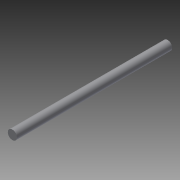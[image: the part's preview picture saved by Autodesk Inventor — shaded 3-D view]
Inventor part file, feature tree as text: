
AUTODESK INVENTOR PART (.ipt)
format: ipt  version: 2014 (Build 180170000, 170)  size: 65,536 bytes
history: native  units: mm
features: extrude x1, sketch x1
ambient origin geometry x8: Origin, YZ Plane, XZ Plane, XY Plane, X Axis, Y Axis, Z Axis, Center Point
bodies: Solid1 (feature_tree)
feature tree (2):
  extrude  "Extrusion1"  Depth=170.0mm TaperAngle=0.0deg
  sketch  "Sketch1"  dims[d0=10.0mm d1=170.0mm d2=0.0mm]
